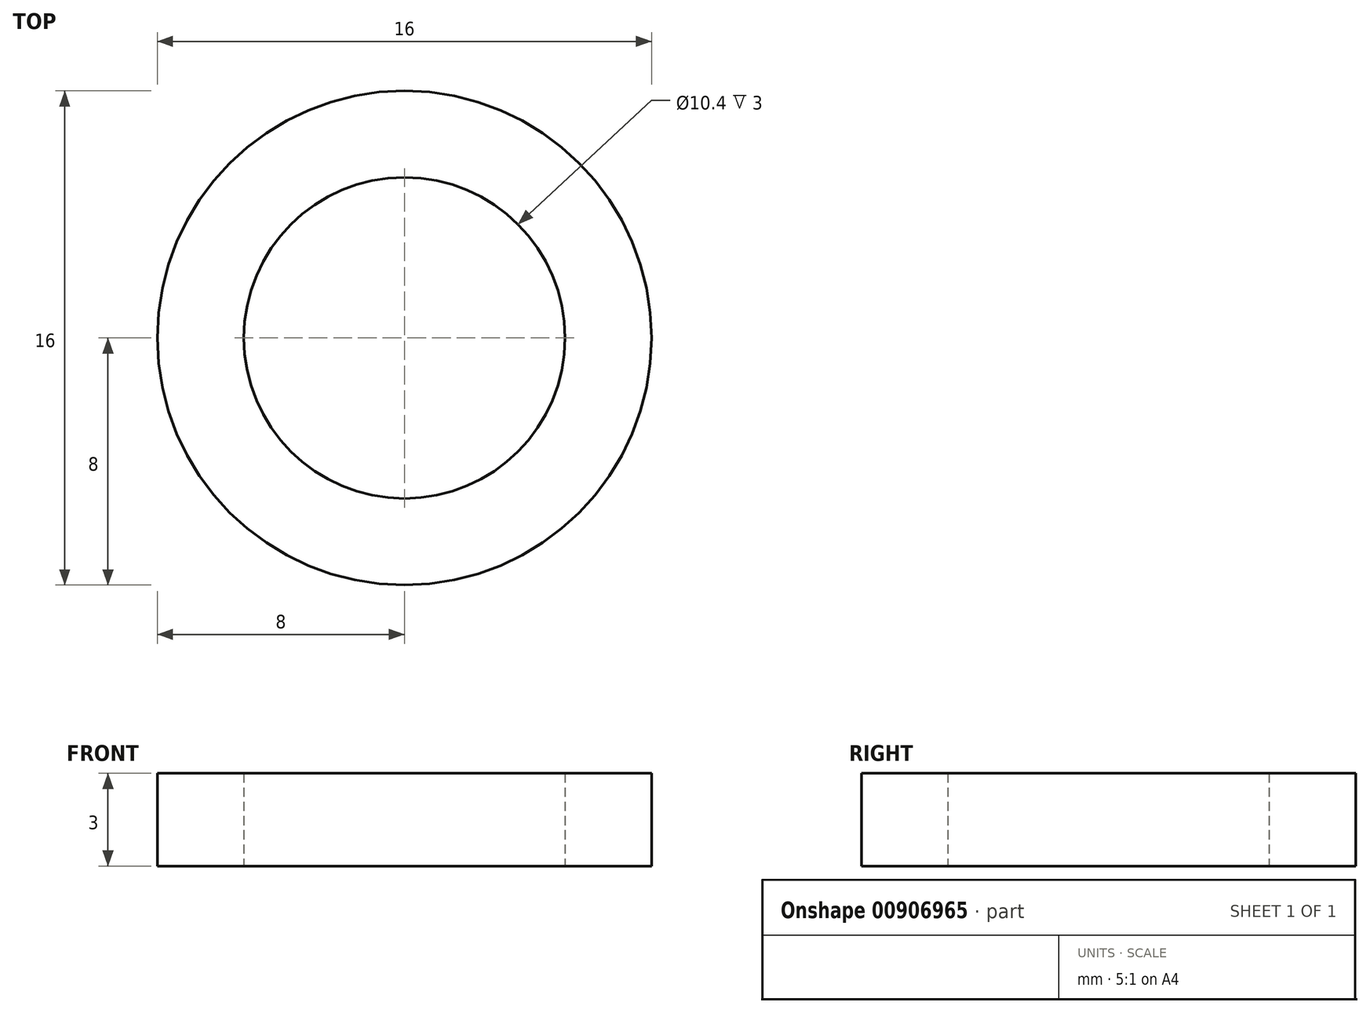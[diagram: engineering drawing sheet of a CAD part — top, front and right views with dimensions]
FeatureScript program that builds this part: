
annotation { "Feature Type Name" : "Feature", "Feature Type Description" : "" }
export const myFeature = defineFeature(function(context is Context, id is Id, definition is map)
    precondition{}
    {
        {
            var Q0;
            Q0=qCreatedBy(makeId("Top.planeOp"),FACE);
            var sketch = newSketch(context, id + "F0", { "sketchPlane" : qUnion([Q0])});
            skCircle(sketch, "E0", {"center": v(0, 0) * mm, "radius": 5.2 * mm});
            skCircle(sketch, "E1", {"center": v(0, 0) * mm, "radius": 8 * mm});
            skSolve(sketch);
        }
        {
            var Q0;
            Q0=makeQuery(id+"F0.imprint","IMPRINT",FACE,{"disambiguationData":[TD([[makeQuery(id+"F0.imprint","IMPRINT",EDGE,{"derivedFrom":sQuery(id+"F0.wireOp",EDGE,"E0")}),-1.0]])]});
            extrude(context, id + "F1", {"entities" : qUnion([Q0]), "depth" : 3 * mm, "offsetDistance" : 25 * mm});
        }
    });
